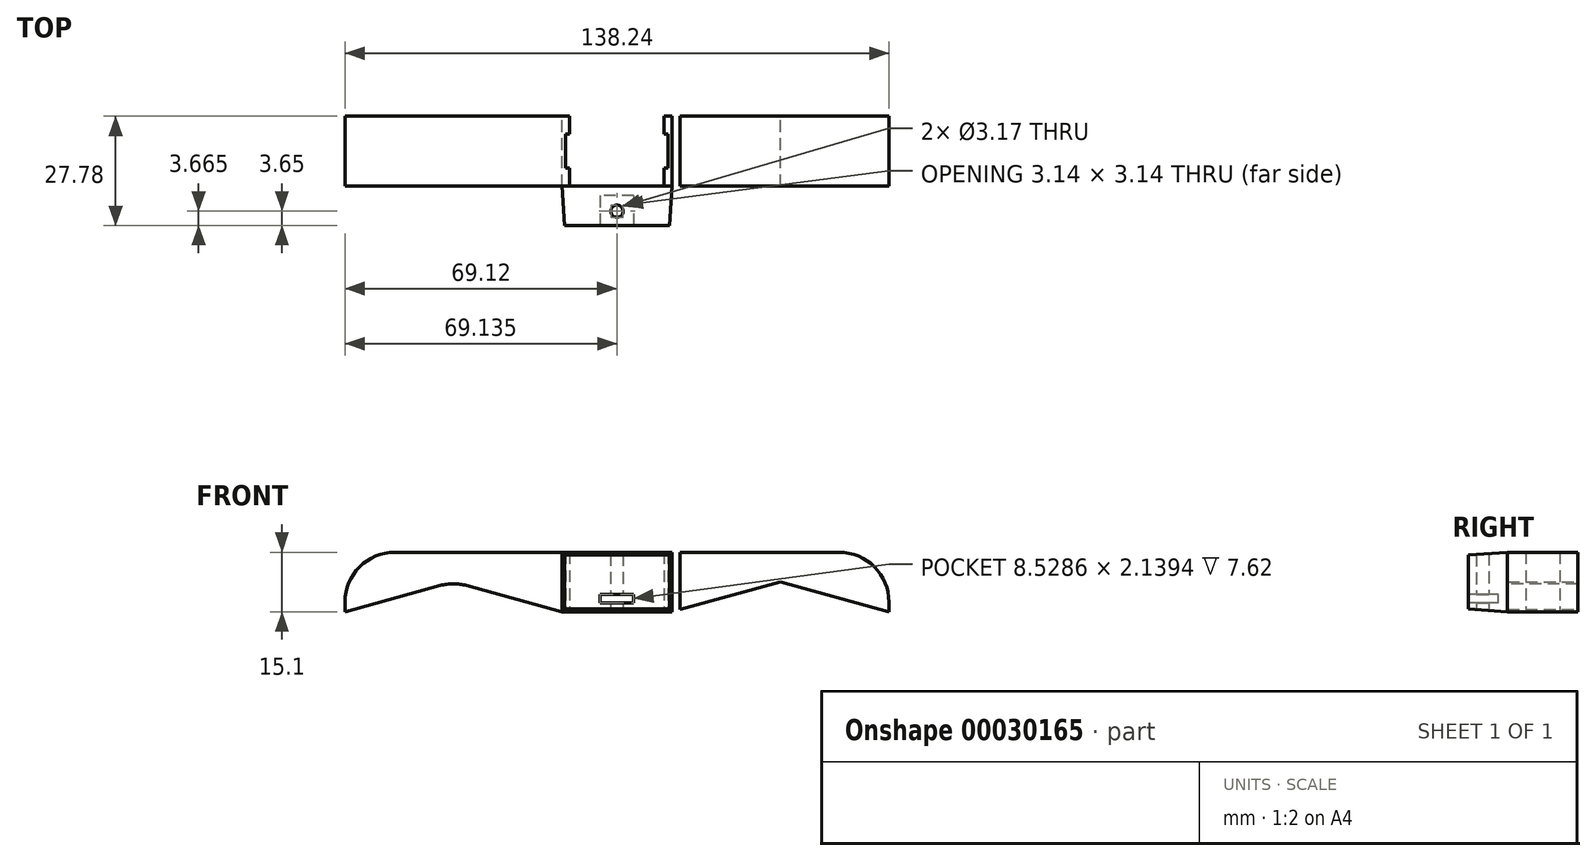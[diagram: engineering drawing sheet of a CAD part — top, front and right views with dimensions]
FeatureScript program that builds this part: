
annotation { "Feature Type Name" : "Feature", "Feature Type Description" : "" }
export const myFeature = defineFeature(function(context is Context, id is Id, definition is map)
    precondition{}
    {
        {
            var Q0;
            Q0=qCreatedBy(makeId("Front.planeOp"),FACE);
            var sketch = newSketch(context, id + "F0", { "sketchPlane" : qUnion([Q0])});
            skLineSegment(sketch, "E0.rect.bottom", {"start": v(0, 0) * mm, "end": v(-14, 0) * mm});
            skLineSegment(sketch, "E0.rect.top", {"start": v(0, 15.1) * mm, "end": v(-14, 15.1) * mm});
            skLineSegment(sketch, "E0.rect.right", {"start": v(-14, 0) * mm, "end": v(-14, 15.1) * mm});
            skPoint(sketch, "E0.rect.middle", {"position": v(0, 7.55) * mm});
            skLineSegment(sketch, "E1.top", {"start": v(-14, 15.1) * mm, "end": v(-56.42, 15.1) * mm});
            skLineSegment(sketch, "E1.right", {"start": v(-69.12, 0) * mm, "end": v(-69.12, 2.4) * mm});
            skLineSegment(sketch, "E2", {"start": v(-69.12, 0) * mm, "end": v(-41.56, 7.55) * mm});
            skLineSegment(sketch, "E3", {"start": v(-41.56, 7.55) * mm, "end": v(-14, 0) * mm});
            skPoint(sketch, "E4.visualSharp", {"position": v(-69.12, 15.1) * mm});
            skArc(sketch, "E4.filletArc", {"start": v(-56.42, 15.1) * mm, "mid": v(-65.4, 11.38) * mm, "end": v(-69.12, 2.4) * mm});
            skPoint(sketch, "E5.orphan", {"position": v(-41.56, 0) * mm});
            skPoint(sketch, "E6.end.orphan", {"position": v(-41.56, 15.1) * mm});
            skPoint(sketch, "E7.orphan", {"position": v(0, 15.1) * mm});
            skLineSegment(sketch, "E8", {"start": v(-16, 15.1) * mm, "end": v(-16, 0.55) * mm});
            skLineSegment(sketch, "E9", {"start": v(0, 15.1) * mm, "end": v(0, 0) * mm});
            skPoint(sketch, "E10.orphan", {"position": v(14, 0) * mm});
            skLineSegment(sketch, "E11.MirrorCS", {"start": v(69.12, 0) * mm, "end": v(69.12, 2.4) * mm});
            skLineSegment(sketch, "E12.MirrorCS", {"start": v(14, 0) * mm, "end": v(14, 15.1) * mm});
            skPoint(sketch, "E13.MirrorP", {"position": v(41.56, 15.1) * mm});
            skLineSegment(sketch, "E14.MirrorCS", {"start": v(69.12, 0) * mm, "end": v(41.56, 7.55) * mm});
            skLineSegment(sketch, "E15.MirrorCS", {"start": v(0, 0) * mm, "end": v(14, 0) * mm});
            skLineSegment(sketch, "E16.MirrorCS", {"start": v(14, 15.1) * mm, "end": v(56.42, 15.1) * mm});
            skLineSegment(sketch, "E17.MirrorCS", {"start": v(0, 15.1) * mm, "end": v(14, 15.1) * mm});
            skPoint(sketch, "E18.MirrorP", {"position": v(69.12, 15.1) * mm});
            skArc(sketch, "E19.MirrorCS", {"start": v(56.42, 15.1) * mm, "mid": v(65.4, 11.38) * mm, "end": v(69.12, 2.4) * mm});
            skPoint(sketch, "E20.MirrorP", {"position": v(41.56, 0) * mm});
            skLineSegment(sketch, "E21.MirrorCS", {"start": v(41.56, 7.55) * mm, "end": v(14, 0) * mm});
            skLineSegment(sketch, "E22.MirrorCS", {"start": v(16, 15.1) * mm, "end": v(16, 0.55) * mm});
            skSolve(sketch);
        }
        {
            var Q0;
            Q0=makeQuery(id+"F0.imprint","IMPRINT",FACE,{"disambiguationData":[TD([[makeQuery(id+"F0.imprint","IMPRINT",EDGE,{"derivedFrom":sQuery(id+"F0.wireOp",EDGE,"E1.top")}),1.0]])]});
            var Q1;
            Q1=makeQuery(id+"F0.imprint","IMPRINT",FACE,{"disambiguationData":[TD([[makeQuery(id+"F0.imprint","IMPRINT",EDGE,{"derivedFrom":sQuery(id+"F0.wireOp",EDGE,"db397d22-fc9e-40e2-9671-9a89a94bb3940.MirrorCS")}),1.0]])]});
            var Q2;
            Q2=makeQuery(id+"F0.imprint","IMPRINT",FACE,{"disambiguationData":[TD([[makeQuery(id+"F0.imprint","IMPRINT",EDGE,{"derivedFrom":sQuery(id+"F0.wireOp",EDGE,"E0.rect.bottom")}),-1.0]])]});
            var Q3;
            Q3=makeQuery(id+"F0.imprint","IMPRINT",FACE,{"disambiguationData":[TD([[makeQuery(id+"F0.imprint","IMPRINT",EDGE,{"derivedFrom":sQuery(id+"F0.wireOp",EDGE,"E1.right")}),-1.0]])]});
            var Q4;
            Q4=makeQuery(id+"F0.imprint","IMPRINT",FACE,{"disambiguationData":[TD([[makeQuery(id+"F0.imprint","IMPRINT",EDGE,{"derivedFrom":sQuery(id+"F0.wireOp",EDGE,"E9")}),1.0]])]});
            var Q5;
            Q5=makeQuery(id+"F0.imprint","IMPRINT",FACE,{"disambiguationData":[TD([[makeQuery(id+"F0.imprint","IMPRINT",EDGE,{"derivedFrom":sQuery(id+"F0.wireOp",EDGE,"E11.MirrorCS")}),1.0]])]});
            var Q6;
            {var subQ0=sQuery(id+"F0.wireOp",EDGE,"E12.MirrorCS");Q6=makeQuery(id+"F0.imprint","IMPRINT",FACE,{"disambiguationData":[TD([[makeQuery(id+"F0.imprint","IMPRINT",EDGE,{"derivedFrom":subQ0}),-1.0]])]});}
            extrude(context, id + "F1", {"entities" : qUnion([Q0, Q1, Q2, Q3, Q4, Q5, Q6]), "depth" : 17.78 * mm});
        }
        {
            var Q0;
            Q0=makeQuery(id+"F1.opExtrude","CAP_FACE",FACE,{"disambiguationData":[OSD([sQuery(id+"F0.wireOp",EDGE,"E0.rect.bottom"),sQuery(id+"F0.wireOp",EDGE,"E0.rect.top"),sQuery(id+"F0.wireOp",EDGE,"E0.rect.right"),sQuery(id+"F0.wireOp",EDGE,"E1.top"),sQuery(id+"F0.wireOp",EDGE,"E1.right"),sQuery(id+"F0.wireOp",EDGE,"E2"),sQuery(id+"F0.wireOp",EDGE,"E3"),sQuery(id+"F0.wireOp",EDGE,"E4.filletArc"),sQuery(id+"F0.wireOp",EDGE,"db397d22-fc9e-40e2-9671-9a89a94bb3940.MirrorCS"),sQuery(id+"F0.wireOp",EDGE,"db397d22-fc9e-40e2-9671-9a89a94bb3941.MirrorCS"),sQuery(id+"F0.wireOp",EDGE,"db397d22-fc9e-40e2-9671-9a89a94bb3943.MirrorCS"),sQuery(id+"F0.wireOp",EDGE,"db397d22-fc9e-40e2-9671-9a89a94bb3944.MirrorCS"),sQuery(id+"F0.wireOp",EDGE,"db397d22-fc9e-40e2-9671-9a89a94bb3945.MirrorCS"),sQuery(id+"F0.wireOp",EDGE,"db397d22-fc9e-40e2-9671-9a89a94bb3948.MirrorCS")])],"isStart":false});
            var sketch = newSketch(context, id + "F2", { "sketchPlane" : qUnion([Q0])});
            skLineSegment(sketch, "E23", {"start": v(-14, 0) * mm, "end": v(-14, 15.1) * mm});
            skLineSegment(sketch, "E24.bottom", {"start": v(-14, 0) * mm, "end": v(14, 0) * mm});
            skLineSegment(sketch, "E24.top", {"start": v(-14, 15.1) * mm, "end": v(14, 15.1) * mm});
            skLineSegment(sketch, "E24.right", {"start": v(14, 0) * mm, "end": v(14, 15.1) * mm});
            skSolve(sketch);
        }
        {
            var Q0;
            Q0=makeQuery(id+"F2.imprint","IMPRINT",FACE,{"disambiguationData":[TD([[makeQuery(id+"F2.imprint","IMPRINT",EDGE,{"derivedFrom":sQuery(id+"F2.wireOp",EDGE,"E24.bottom")}),-1.0]])]});
            extrude(context, id + "F3", {"entities" : qUnion([Q0]), "operationType" : NewBodyOperationType.ADD, "depth" : 10 * mm, "hasDraft" : true, "draftAngle" : 4 * degree, "draftPullDirection" : true});
        }
        {
            var Q0;
            Q0=makeQuery(id+"F1.opExtrude","SWEPT_EDGE",EDGE,{"disambiguationData":[OSD([sQuery(id+"F0.wireOp",EDGE,"E2"),sQuery(id+"F0.wireOp",EDGE,"E3")])]});
            var Q1;
            Q1=makeQuery(id+"F1.opExtrude","SWEPT_EDGE",EDGE,{"disambiguationData":[OSD([sQuery(id+"F0.wireOp",EDGE,"db397d22-fc9e-40e2-9671-9a89a94bb3943.MirrorCS"),sQuery(id+"F0.wireOp",EDGE,"db397d22-fc9e-40e2-9671-9a89a94bb3945.MirrorCS")])]});
            var Q2;
            Q2=makeQuery(id+"FLix7vaN4n2k8BL_1.opShell","OFFSET_EDGE",EDGE,{"disambiguationData":[OSD([sQuery(id+"F0.wireOp",EDGE,"E2"),sQuery(id+"F0.wireOp",EDGE,"E3")])]});
            var Q3;
            Q3=makeQuery(id+"FLix7vaN4n2k8BL_1.opShell","OFFSET_EDGE",EDGE,{"disambiguationData":[OSD([sQuery(id+"F0.wireOp",EDGE,"db397d22-fc9e-40e2-9671-9a89a94bb3943.MirrorCS"),sQuery(id+"F0.wireOp",EDGE,"db397d22-fc9e-40e2-9671-9a89a94bb3945.MirrorCS")])]});
            fillet(context, id + "F4", {"entities" : qUnion([Q0, Q1, Q2, Q3]), "radius" : 12.7 * mm, "tangentPropagation" : true, "allowEdgeOverflow" : false});
        }
        {
            var Q0;
            Q0=makeQuery(id+"F1.opExtrude","SWEPT_FACE",FACE,{"disambiguationData":[OSD([sQuery(id+"F0.wireOp",EDGE,"E0.rect.bottom"),sQuery(id+"F0.wireOp",EDGE,"E15.MirrorCS")])]});
            var sketch = newSketch(context, id + "F5", { "sketchPlane" : qUnion([Q0])});
            skLineSegment(sketch, "E25.rect.bottom", {"start": v(12, 0) * mm, "end": v(-12, 0) * mm});
            skLineSegment(sketch, "E25.rect.top", {"start": v(12, 17.74) * mm, "end": v(-12, 17.74) * mm});
            skLineSegment(sketch, "E25.rect.left", {"start": v(12, 0) * mm, "end": v(12, 17.74) * mm});
            skLineSegment(sketch, "E25.rect.right", {"start": v(-12, 0) * mm, "end": v(-12, 17.74) * mm});
            skPoint(sketch, "E25.rect.middle", {"position": v(0, 8.87) * mm});
            skLineSegment(sketch, "E26.rect.bottom", {"start": v(13, 13.17) * mm, "end": v(-13, 13.17) * mm});
            skLineSegment(sketch, "E26.rect.top", {"start": v(13, 4.57) * mm, "end": v(-13, 4.57) * mm});
            skLineSegment(sketch, "E26.rect.left", {"start": v(13, 13.17) * mm, "end": v(13, 4.57) * mm});
            skLineSegment(sketch, "E26.rect.right", {"start": v(-13, 13.17) * mm, "end": v(-13, 4.57) * mm});
            skCircle(sketch, "E27", {"center": v(0, 24.13) * mm, "radius": 1.59 * mm});
            skSolve(sketch);
        }
        {
            var Q0;
            {var subQ0=sQuery(id+"F5.wireOp",EDGE,"E26.rect.right");Q0=makeQuery(id+"F5.imprint","IMPRINT",FACE,{"disambiguationData":[TD([[makeQuery(id+"F5.imprint","IMPRINT",EDGE,{"derivedFrom":subQ0}),1.0]])]});}
            var Q1;
            {var subQ0=sQuery(id+"F5.wireOp",EDGE,"E26.rect.top");var subQ3=sQuery(id+"F5.wireOp",EDGE,"E25.rect.left");var subQ4=makeQuery(id+"F5.imprint","INTERSECT",VERTEX,{"derivedFrom":[subQ3,subQ0]});Q1=makeQuery(id+"F5.imprint","IMPRINT",FACE,{"disambiguationData":[TD([[makeQuery(id+"F5.imprint","IMPRINT",EDGE,{"disambiguationData":[TD([[subQ4,-1.0]])],"derivedFrom":subQ3}),1.0]])]});}
            var Q2;
            {var subQ6=sQuery(id+"F5.wireOp",EDGE,"E25.rect.bottom");Q2=makeQuery(id+"F5.imprint","IMPRINT",FACE,{"disambiguationData":[TD([[makeQuery(id+"F5.imprint","IMPRINT",EDGE,{"derivedFrom":subQ6}),-1.0]])]});}
            var Q3;
            {var subQ0=sQuery(id+"F5.wireOp",EDGE,"E26.rect.left");Q3=makeQuery(id+"F5.imprint","IMPRINT",FACE,{"disambiguationData":[TD([[makeQuery(id+"F5.imprint","IMPRINT",EDGE,{"derivedFrom":subQ0}),-1.0]])]});}
            var Q4;
            {var subQ5=sQuery(id+"F5.wireOp",EDGE,"E25.rect.top");Q4=makeQuery(id+"F5.imprint","IMPRINT",FACE,{"disambiguationData":[TD([[makeQuery(id+"F5.imprint","IMPRINT",EDGE,{"derivedFrom":subQ5}),1.0]])]});}
            var Q5;
            Q5=makeQuery(id+"F5.imprint","IMPRINT",FACE,{"disambiguationData":[TD([[makeQuery(id+"F5.imprint","IMPRINT",EDGE,{"derivedFrom":sQuery(id+"F5.wireOp",EDGE,"E27")}),1.0]])]});
            extrude(context, id + "F6", {"entities" : qUnion([Q0, Q1, Q2, Q3, Q4, Q5]), "operationType" : NewBodyOperationType.REMOVE, "endBound" : BoundingType.THROUGH_ALL, "oppositeDirection" : true, "depth" : 25.4 * mm});
        }
        {
            var Q0;
            Q0=makeQuery(id+"F3.opExtrude","CAP_FACE",FACE,{"disambiguationData":[OSD([sQuery(id+"F2.wireOp",EDGE,"E24.bottom"),sQuery(id+"F2.wireOp",EDGE,"E24.top"),sQuery(id+"F2.wireOp",EDGE,"E23"),sQuery(id+"F2.wireOp",EDGE,"E24.right")])],"isStart":false});
            var sketch = newSketch(context, id + "F7", { "sketchPlane" : qUnion([Q0])});
            skLineSegment(sketch, "E28.rect.bottom", {"start": v(4.26, 2.26) * mm, "end": v(-4.26, 2.26) * mm});
            skLineSegment(sketch, "E28.rect.top", {"start": v(4.26, 4.4) * mm, "end": v(-4.26, 4.4) * mm});
            skLineSegment(sketch, "E28.rect.left", {"start": v(4.26, 2.26) * mm, "end": v(4.26, 4.4) * mm});
            skLineSegment(sketch, "E28.rect.right", {"start": v(-4.26, 2.26) * mm, "end": v(-4.26, 4.4) * mm});
            skPoint(sketch, "E28.rect.middle", {"position": v(0, 3.33) * mm});
            skSolve(sketch);
        }
        {
            var Q0;
            Q0=makeQuery(id+"F7.imprint","IMPRINT",FACE,{"disambiguationData":[TD([[makeQuery(id+"F7.imprint","IMPRINT",EDGE,{"derivedFrom":sQuery(id+"F7.wireOp",EDGE,"E28.rect.bottom")}),-1.0]])]});
            extrude(context, id + "F8", {"entities" : qUnion([Q0]), "operationType" : NewBodyOperationType.REMOVE, "oppositeDirection" : true, "depth" : 7.62 * mm});
        }
    });
